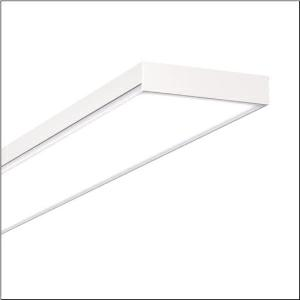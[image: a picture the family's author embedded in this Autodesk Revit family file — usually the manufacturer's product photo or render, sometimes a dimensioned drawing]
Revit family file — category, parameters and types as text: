
# Revit family: apollon_31_surface_51mp26wm2341w
name_source: partatom
category: Lighting Fixtures
units: mm (PartAtom-declared; Revit-internal decimal feet)

## family parameters
Cut with Voids When Loaded = No
Host = Face
Light Source = No
Part Type = Normal
Room Calculation Point = No
Round Connector Dimension = Use Diameter
Shared = No

## types (1)
- Apollon 31 Surface (1 x LED, 4400 lm, 33 W, 3000K)
    Apparent Load = 33 VA
    CIE Flux Codes = 61 87 97 97 100
    Color Rendering = 80
    Color Temperature = 3000K
    Default Elevation = 1800 mm
    Description = Apollon 31 Surface, office luminaire, primary optical cover: micro prismatic cover, of PMMA, light emission: direct distribution, primary light characteristic: symmetric, installation type: surface-mounted, LED, rated luminous flux: 4.400lm, luminous efficacy: 133lm/W, light colour: 830, colour temperature: 3000K, control gear: ON/OFF Multilumen, with terminal, 3-pole, mains connection: 220..240V, AC, 50/60Hz, rated input power: 33W, housing, of sheet steel, coated, traffic white (RAL 9016), length: 1.545mm, width: 200mm, height: 44mm, protection rating (complete): IP20, protection rating (on room side): IP40, protection rating (lamp compartment, on room side): IP40, insulation class (complete): insulation class I (protective earthing), certification: CE, ENEC, UKCA, impact resistance: IK02, permissible operating ambient temperature: -20..+40°C, packaging unit: 1 piece
    Height = 44 mm
    Lamp = 1 x LED
    Lamp Light Flux = 4400 lm
    Lamp Power = 33 W
    Lamp count = 1
    Length = 1545 mm
    Luminous efficacy = 133 lm/W
    Manufacturer = Siteco
    ModVariant = No
    Model = 51MP26WM2341W
    Mounting Place = Ceiling
    Mounting Type = Surface mounted
    Number of Poles = 1
    OnlyDefault = Yes
    Power Factor = 1
    Product Name = Apollon 31 Surface
    Product group = office luminaire | ceiling mounted
    ProductGroupID = 301
    Protection Class = Protection class I
    Protection Degree = IP 20
    RLX_Detail_Level = 1
    RLX_Emergency_Light_Flux = 0 lm
    RLX_Emergency_Type = 0
    RLX_Emergency_Type_DB = No
    RlxData = <blob elided: 20801 chars, md5=ba0f77c3>
    Socket = socket
    Standby Power = 0 W
    System Light Flux = 4400 lm
    System Power = 33 W
    Type Comments = Product without accessories
    Type Image = l_1313658.jpg
    URL = http://relux.com
    VarID = ---
    Voltage = 0 V
    Weight = 0.00 kg
    Width = 200 mm  [stored 0.656168 ft]

note: [stored X ft] marks values corroborated as IEEE doubles in the binary element streams (Revit-internal decimal feet)

## geometry (parser evidence)
native form markers: Blend x4, Sweep x11
no freeform markers — native parametric forms only
